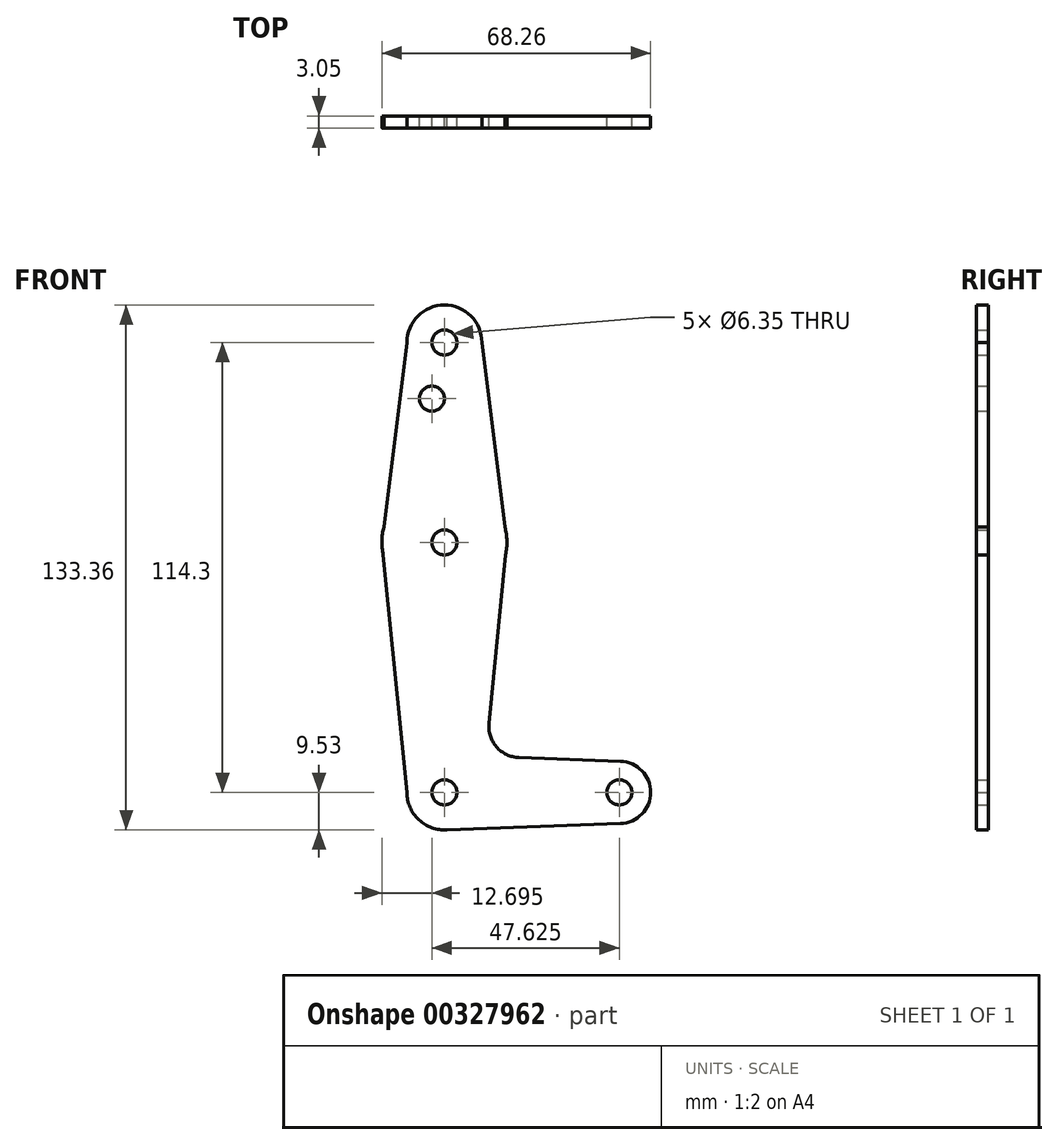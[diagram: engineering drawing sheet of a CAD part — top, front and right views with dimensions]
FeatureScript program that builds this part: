
annotation { "Feature Type Name" : "Feature", "Feature Type Description" : "" }
export const myFeature = defineFeature(function(context is Context, id is Id, definition is map)
    precondition{}
    {
        {
            var Q0;
            Q0=qCreatedBy(makeId("Front.planeOp"),FACE);
            var sketch = newSketch(context, id + "F0", { "sketchPlane" : qUnion([Q0])});
            skLineSegment(sketch, "E0", {"start": v(0, 0) * mm, "end": v(0, 114.3) * mm, "construction": true});
            skLineSegment(sketch, "E1", {"start": v(44.45, 0) * mm, "end": v(0, 0) * mm, "construction": true});
            skCircle(sketch, "E2", {"center": v(0, 114.3) * mm, "radius": 9.53 * mm});
            skCircle(sketch, "E3", {"center": v(0, 0) * mm, "radius": 9.53 * mm});
            skCircle(sketch, "E4", {"center": v(44.45, 0) * mm, "radius": 7.94 * mm});
            skCircle(sketch, "E5", {"center": v(0, 63.5) * mm, "radius": 15.88 * mm});
            skLineSegment(sketch, "E6", {"start": v(9.52, 114.3) * mm, "end": v(15.88, 63.5) * mm});
            skLineSegment(sketch, "E7", {"start": v(15.88, 63.5) * mm, "end": v(11.32, 17.58) * mm});
            skLineSegment(sketch, "E8", {"start": v(0, -9.53) * mm, "end": v(44.73, -7.93) * mm});
            skLineSegment(sketch, "E9", {"start": v(-9.52, 114.3) * mm, "end": v(-15.88, 63.5) * mm});
            skCircle(sketch, "E10", {"center": v(0, 114.3) * mm, "radius": 3.18 * mm});
            skCircle(sketch, "E11", {"center": v(-3.18, 100.03) * mm, "radius": 3.18 * mm});
            skCircle(sketch, "E12", {"center": v(0, 63.5) * mm, "radius": 3.18 * mm});
            skCircle(sketch, "E13", {"center": v(0, 0) * mm, "radius": 3.18 * mm});
            skCircle(sketch, "E14", {"center": v(44.45, 0) * mm, "radius": 3.18 * mm});
            skLineSegment(sketch, "E15", {"start": v(18.95, 8.85) * mm, "end": v(44.73, 7.93) * mm});
            skArc(sketch, "E16.filletArc", {"start": v(11.32, 17.58) * mm, "mid": v(13.24, 11.56) * mm, "end": v(18.95, 8.85) * mm});
            skLineSegment(sketch, "E17", {"start": v(-9.52, 0) * mm, "end": v(-15.88, 63.5) * mm});
            skSolve(sketch);
        }
        {
            var Q0;
            Q0 = qSketchRegion(id + "F0", true);
            extrude(context, id + "F1", {"entities" : qUnion([Q0]), "depth" : 3.05 * mm});
        }
    });
